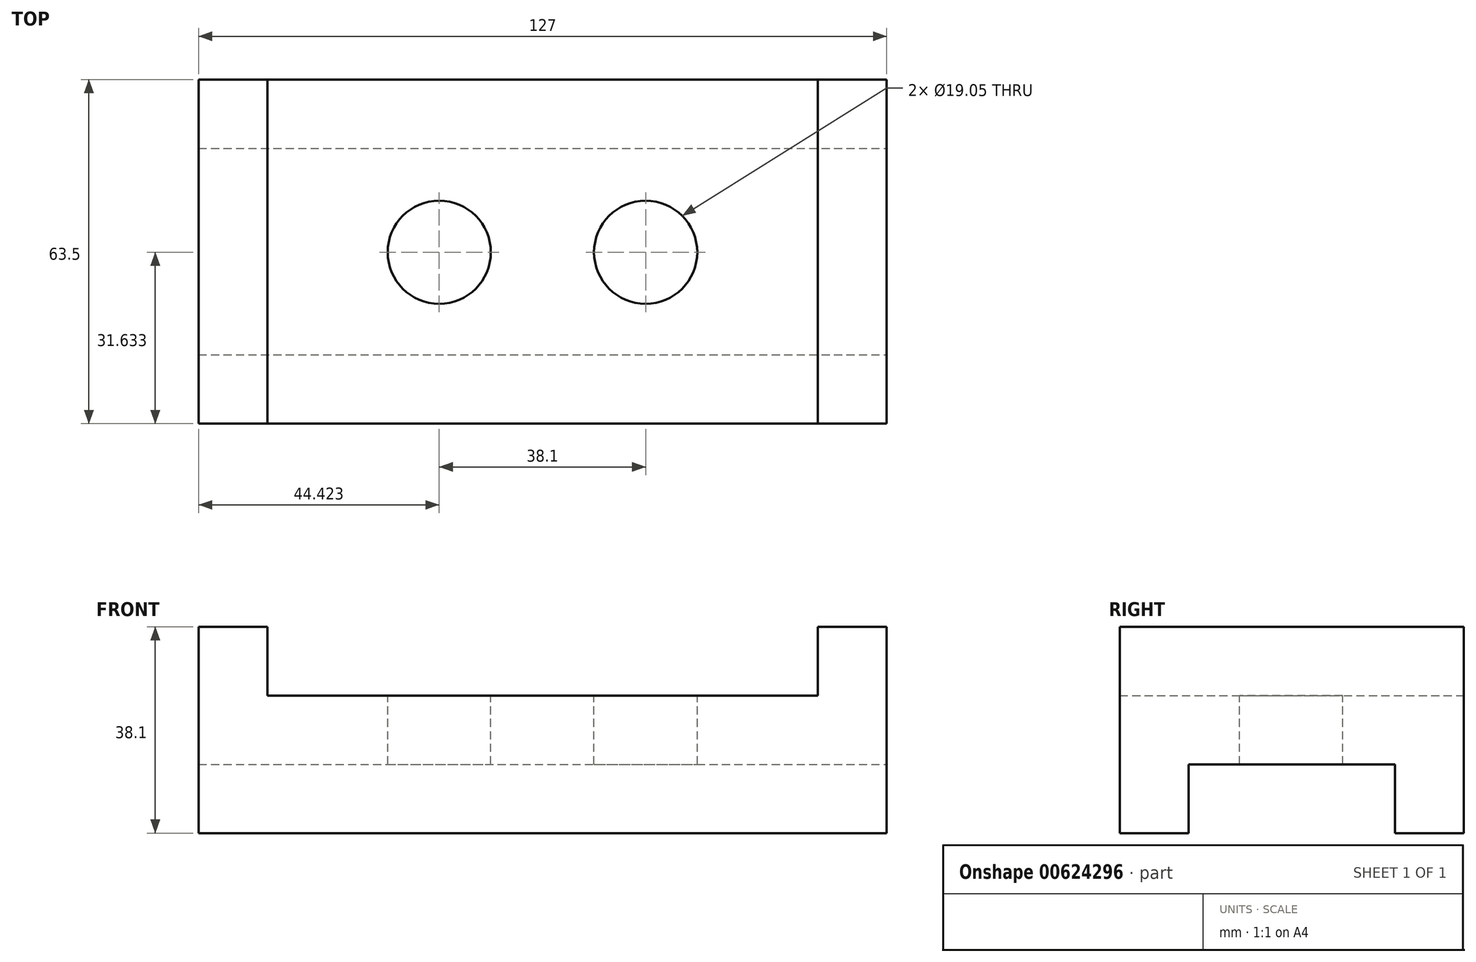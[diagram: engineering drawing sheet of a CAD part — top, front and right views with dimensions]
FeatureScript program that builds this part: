
annotation { "Feature Type Name" : "Feature", "Feature Type Description" : "" }
export const myFeature = defineFeature(function(context is Context, id is Id, definition is map)
    precondition{}
    {
        {
            var Q0;
            Q0=qCreatedBy(makeId("Top.planeOp"),FACE);
            var sketch = newSketch(context, id + "F0", { "sketchPlane" : qUnion([Q0])});
            skLineSegment(sketch, "E0.bottom", {"start": v(-54.37, -52.1) * mm, "end": v(72.63, -52.1) * mm});
            skLineSegment(sketch, "E0.top", {"start": v(-54.37, 11.4) * mm, "end": v(72.63, 11.4) * mm});
            skLineSegment(sketch, "E0.left", {"start": v(-54.37, -52.1) * mm, "end": v(-54.37, 11.4) * mm});
            skLineSegment(sketch, "E0.right", {"start": v(72.63, -52.1) * mm, "end": v(72.63, 11.4) * mm});
            skSolve(sketch);
        }
        {
            var Q0;
            Q0=makeQuery(id+"F0.imprint","IMPRINT",FACE,{"disambiguationData":[TD([[makeQuery(id+"F0.imprint","IMPRINT",EDGE,{"derivedFrom":sQuery(id+"F0.wireOp",EDGE,"E0.bottom")}),1.0]])]});
            extrude(context, id + "F1", {"entities" : qUnion([Q0]), "depth" : 25.4 * mm, "offsetDistance" : 25.4 * mm});
        }
        {
            var Q0;
            Q0=makeQuery(id+"F1.opExtrude","CAP_FACE",FACE,{"disambiguationData":[OSD([sQuery(id+"F0.wireOp",EDGE,"E0.bottom"),sQuery(id+"F0.wireOp",EDGE,"E0.top"),sQuery(id+"F0.wireOp",EDGE,"E0.left"),sQuery(id+"F0.wireOp",EDGE,"E0.right")])],"isStart":false});
            var sketch = newSketch(context, id + "F2", { "sketchPlane" : qUnion([Q0])});
            skLineSegment(sketch, "E1", {"start": v(-54.37, -52.1) * mm, "end": v(-41.67, -52.1) * mm});
            skLineSegment(sketch, "E2", {"start": v(-41.67, -52.1) * mm, "end": v(-41.67, 11.4) * mm});
            skLineSegment(sketch, "E3", {"start": v(-41.67, 11.4) * mm, "end": v(-54.37, 11.4) * mm});
            skLineSegment(sketch, "E4", {"start": v(-54.37, 11.4) * mm, "end": v(-54.37, -52.1) * mm});
            skSolve(sketch);
        }
        {
            var Q0;
            Q0=makeQuery(id+"F2.imprint","IMPRINT",FACE,{"disambiguationData":[TD([[makeQuery(id+"F2.imprint","IMPRINT",EDGE,{"derivedFrom":sQuery(id+"F2.wireOp",EDGE,"E1")}),1.0]])]});
            extrude(context, id + "F3", {"entities" : qUnion([Q0]), "operationType" : NewBodyOperationType.ADD, "depth" : 12.7 * mm, "offsetDistance" : 25.4 * mm});
        }
        {
            var Q0;
            Q0=makeQuery(id+"F1.opExtrude","CAP_FACE",FACE,{"disambiguationData":[OSD([sQuery(id+"F0.wireOp",EDGE,"E0.bottom"),sQuery(id+"F0.wireOp",EDGE,"E0.top"),sQuery(id+"F0.wireOp",EDGE,"E0.left"),sQuery(id+"F0.wireOp",EDGE,"E0.right")])],"isStart":false});
            var sketch = newSketch(context, id + "F4", { "sketchPlane" : qUnion([Q0])});
            skLineSegment(sketch, "E5", {"start": v(72.63, -52.1) * mm, "end": v(59.93, -52.1) * mm});
            skLineSegment(sketch, "E6", {"start": v(59.93, -52.1) * mm, "end": v(59.93, 11.4) * mm});
            skLineSegment(sketch, "E7", {"start": v(59.93, 11.4) * mm, "end": v(72.63, 11.4) * mm});
            skLineSegment(sketch, "E8", {"start": v(72.63, 11.4) * mm, "end": v(72.63, -52.1) * mm});
            skSolve(sketch);
        }
        {
            var Q0;
            Q0=makeQuery(id+"F4.imprint","IMPRINT",FACE,{"disambiguationData":[TD([[makeQuery(id+"F4.imprint","IMPRINT",EDGE,{"derivedFrom":sQuery(id+"F4.wireOp",EDGE,"E5")}),1.0]])]});
            extrude(context, id + "F5", {"entities" : qUnion([Q0]), "operationType" : NewBodyOperationType.ADD, "depth" : 12.7 * mm, "offsetDistance" : 25.4 * mm});
        }
        {
            var Q0;
            Q0=makeQuery(id+"F1.opExtrude","CAP_FACE",FACE,{"disambiguationData":[OSD([sQuery(id+"F0.wireOp",EDGE,"E0.bottom"),sQuery(id+"F0.wireOp",EDGE,"E0.top"),sQuery(id+"F0.wireOp",EDGE,"E0.left"),sQuery(id+"F0.wireOp",EDGE,"E0.right")])],"isStart":false});
            var sketch = newSketch(context, id + "F6", { "sketchPlane" : qUnion([Q0])});
            skCircle(sketch, "E9", {"center": v(-9.95, -20.47) * mm, "radius": 9.53 * mm});
            skCircle(sketch, "E10", {"center": v(28.15, -20.47) * mm, "radius": 9.53 * mm});
            skSolve(sketch);
        }
        {
            var Q0;
            Q0=makeQuery(id+"F6.imprint","IMPRINT",FACE,{"disambiguationData":[TD([[makeQuery(id+"F6.imprint","IMPRINT",EDGE,{"derivedFrom":sQuery(id+"F6.wireOp",EDGE,"E9")}),1.0]])]});
            var Q1;
            Q1=makeQuery(id+"F6.imprint","IMPRINT",FACE,{"disambiguationData":[TD([[makeQuery(id+"F6.imprint","IMPRINT",EDGE,{"derivedFrom":sQuery(id+"F6.wireOp",EDGE,"E10")}),1.0]])]});
            extrude(context, id + "F7", {"entities" : qUnion([Q0, Q1]), "operationType" : NewBodyOperationType.REMOVE, "endBound" : BoundingType.THROUGH_ALL, "oppositeDirection" : true, "depth" : 25.4 * mm, "offsetDistance" : 25.4 * mm});
        }
        {
            var Q0;
            Q0=makeQuery(id+"F5.boolean.opBoolean","MERGE",FACE,{"derivedFrom":[makeQuery(id+"F1.opExtrude","SWEPT_FACE",FACE,{"disambiguationData":[OSD([sQuery(id+"F0.wireOp",EDGE,"E0.right")])]}),makeQuery(id+"F5.opExtrude","SWEPT_FACE",FACE,{"disambiguationData":[OSD([sQuery(id+"F4.wireOp",EDGE,"E8")])]})]});
            var sketch = newSketch(context, id + "F8", { "sketchPlane" : qUnion([Q0])});
            skLineSegment(sketch, "E11", {"start": v(-52.1, 0) * mm, "end": v(-39.4, 0) * mm});
            skLineSegment(sketch, "E12", {"start": v(-39.4, 0) * mm, "end": v(-39.4, 12.7) * mm});
            skLineSegment(sketch, "E13", {"start": v(-39.4, 12.7) * mm, "end": v(-1.3, 12.7) * mm});
            skLineSegment(sketch, "E14", {"start": v(-1.3, 12.7) * mm, "end": v(-1.3, 0) * mm});
            skLineSegment(sketch, "E15", {"start": v(-1.3, 0) * mm, "end": v(-39.4, 0) * mm});
            skSolve(sketch);
        }
        {
            var Q0;
            Q0=makeQuery(id+"F8.imprint","IMPRINT",FACE,{"disambiguationData":[TD([[makeQuery(id+"F8.imprint","IMPRINT",EDGE,{"derivedFrom":sQuery(id+"F8.wireOp",EDGE,"E12")}),-1.0]])]});
            extrude(context, id + "F9", {"entities" : qUnion([Q0]), "operationType" : NewBodyOperationType.REMOVE, "endBound" : BoundingType.THROUGH_ALL, "oppositeDirection" : true, "depth" : 25.4 * mm, "offsetDistance" : 25.4 * mm});
        }
    });
